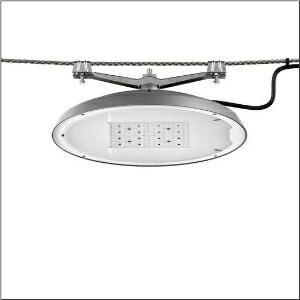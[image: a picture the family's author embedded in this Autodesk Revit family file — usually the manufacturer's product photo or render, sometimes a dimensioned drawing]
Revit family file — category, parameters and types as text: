
# Revit family: dl_r__50_iq_mini___st1_0s_5xa248w21f08me_4099
name_source: partatom
category: Lighting Fixtures
units: mm (PartAtom-declared; Revit-internal decimal feet)

## family parameters
Cut with Voids When Loaded = No
Host = Face
Light Source = No
Part Type = Normal
Room Calculation Point = No
Round Connector Dimension = Use Diameter
Shared = No

## types (1)
- --- (1 x LED, 12600 lm, 103.8 W, 2200K)
    Apparent Load = 104 VA
    CIE Flux Codes = 37 72 97 100 100
    Color Rendering = 70
    Color Temperature = 2200K
    Default Elevation = 1800 mm
    Description = DL® 50 iQ mini, catenary luminaire, primary light control with lens, of PMMA, primary optical cover: cover, of toughened safety glass, transparent, light distribution: ST1.0s, light emission: direct distribution, primary light characteristic: symmetric, installation type: suspended mounting, LED, High Power LED, rated luminous flux: 12.600lm, luminous efficacy: 121lm/W, light colour: 722, colour temperature: 2200K, control gear: iQ Street-Remote, control: optimised constant luminous flux control (CLO 2.0), Desk-Remote (wireless, voltage-free reading and setting of iQ features in the workshop via application-optimized NFC function/RFID function), Light-Fading, Smart-Wire, Night-Set, Lumen-Switch, Temp-Guard, Auto-Match, Street-Remote, mains connection: 230..240V, AC, 50/60Hz, start of lifetime: 104W, end of service life: 114W, reduction: 46W, luminaire housing, of diecast aluminium, powder-coated, Siteco® metallic grey (DB 702S), diameter: 500mm, height: 115mm, mounting height: 4..12m, protection rating (complete): IP66, insulation class (complete): insulation class II (safety insulation), certification: CE, ENEC, ENEC+, VDE, impact resistance: IK08, permissible operating ambient temperature for outdoor applications: -25..+40°C, standard-compliant lighting for roads and squares, packaging unit: 1 piece

Light Distribution: ST1.0s
    Height = 124 mm  [stored 0.406824 ft]
    Lamp = 1 x LED
    Lamp Light Flux = 12600 lm
    Lamp Power = 103.8 W
    Lamp count = 1
    Length = 500 mm
    Luminous efficacy = 121 lm/W
    Manufacturer = Siteco
    ModVariant = No
    Model = 5XA248W21F08ME
    Number of Poles = 1
    OnlyDefault = Yes
    Power Factor = 1
    Product Name = DL® 50 iQ mini | ST1.0s
    Product group = catenary luminaire
    ProductGroupID = 6300
    Protection Class = Protection class II
    Protection Degree = IP 66
    RLX_Detail_Level = 1
    RLX_Emergency_Light_Flux = 0 lm
    RLX_Emergency_Type = 0
    RLX_Emergency_Type_DB = No
    RlxData = <blob elided: 126797 chars, md5=b1fd5f9d>
    Socket = socket
    Standby Power = 0 W
    System Light Flux = 12600 lm
    System Power = 104 W
    Type Comments = factory setting: luminous flux: 100 % | dim-lin: 254 | 545 mA
    Type Image = l_1251783.jpg
    URL = http://relux.com
    VarID = @adj_140450
    Voltage = 0 V
    Weight = 0.00 kg
    Width = 0 mm  [stored 0 ft]

note: [stored X ft] marks values corroborated as IEEE doubles in the binary element streams (Revit-internal decimal feet)

## geometry (parser evidence)
native form markers: Blend x4, Sweep x14
no freeform markers — native parametric forms only
